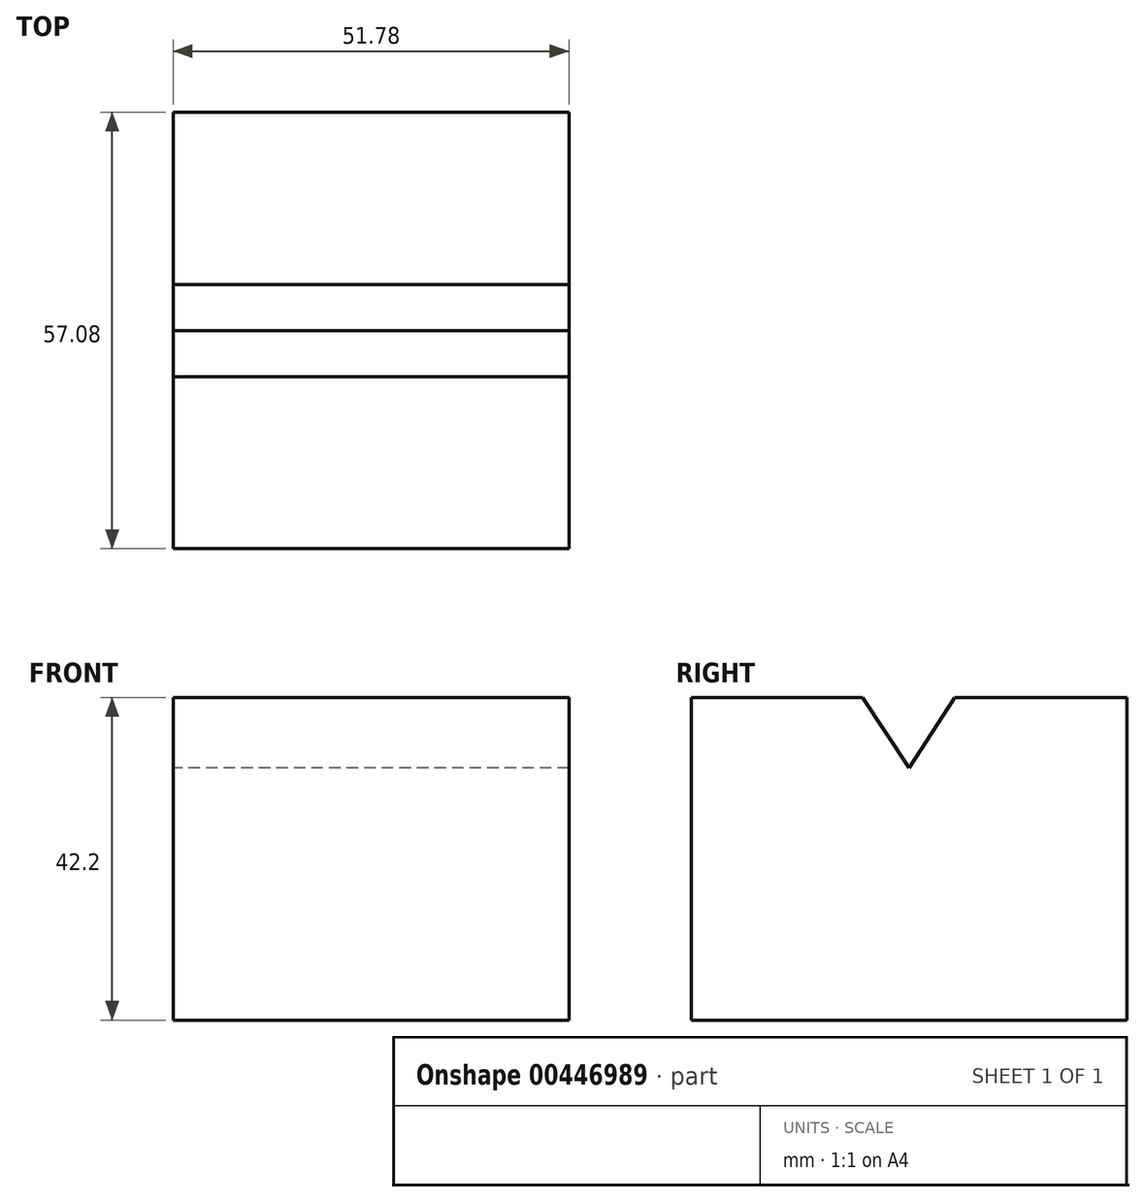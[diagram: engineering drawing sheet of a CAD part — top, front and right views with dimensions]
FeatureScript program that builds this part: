
annotation { "Feature Type Name" : "Feature", "Feature Type Description" : "" }
export const myFeature = defineFeature(function(context is Context, id is Id, definition is map)
    precondition{}
    {
        {
            var Q0;
            Q0=qCreatedBy(makeId("Right.planeOp"),FACE);
            var sketch = newSketch(context, id + "F0", { "sketchPlane" : qUnion([Q0])});
            skLineSegment(sketch, "E0.bottom", {"start": v(28.54, 21.1) * mm, "end": v(-28.54, 21.1) * mm});
            skLineSegment(sketch, "E0.top", {"start": v(28.54, -21.1) * mm, "end": v(-28.54, -21.1) * mm});
            skLineSegment(sketch, "E0.left", {"start": v(28.54, 21.1) * mm, "end": v(28.54, -21.1) * mm});
            skLineSegment(sketch, "E0.right", {"start": v(-28.54, 21.1) * mm, "end": v(-28.54, -21.1) * mm});
            skPoint(sketch, "E0.middle", {"position": v(0, 0) * mm});
            skSolve(sketch);
        }
        {
            var Q0;
            Q0=makeQuery(id+"F0.imprint","IMPRINT",FACE,{"disambiguationData":[TD([[makeQuery(id+"F0.imprint","IMPRINT",EDGE,{"derivedFrom":sQuery(id+"F0.wireOp",EDGE,"E0.bottom")}),1.0]])]});
            extrude(context, id + "F1", {"entities" : qUnion([Q0]), "endBound" : BoundingType.SYMMETRIC, "depth" : 51.8 * mm});
        }
        {
            var Q0;
            Q0=qCreatedBy(makeId("Right.planeOp"),FACE);
            var sketch = newSketch(context, id + "F2", { "sketchPlane" : qUnion([Q0])});
            skLineSegment(sketch, "E1", {"start": v(-20.09, 42.22) * mm, "end": v(0, 11.91) * mm});
            skLineSegment(sketch, "E2", {"start": v(0, 11.91) * mm, "end": v(0, 11.91) * mm});
            skLineSegment(sketch, "E3", {"start": v(19.52, 41.9) * mm, "end": v(0, 11.91) * mm});
            skLineSegment(sketch, "E4", {"start": v(-20.09, 42.22) * mm, "end": v(19.52, 41.9) * mm});
            skSolve(sketch);
        }
        {
            var Q0;
            Q0 = qSketchRegion(id + "F2", true);
            extrude(context, id + "F3", {"entities" : qUnion([Q0]), "operationType" : NewBodyOperationType.REMOVE, "endBound" : BoundingType.SYMMETRIC, "depth" : 80 * mm});
        }
    });
